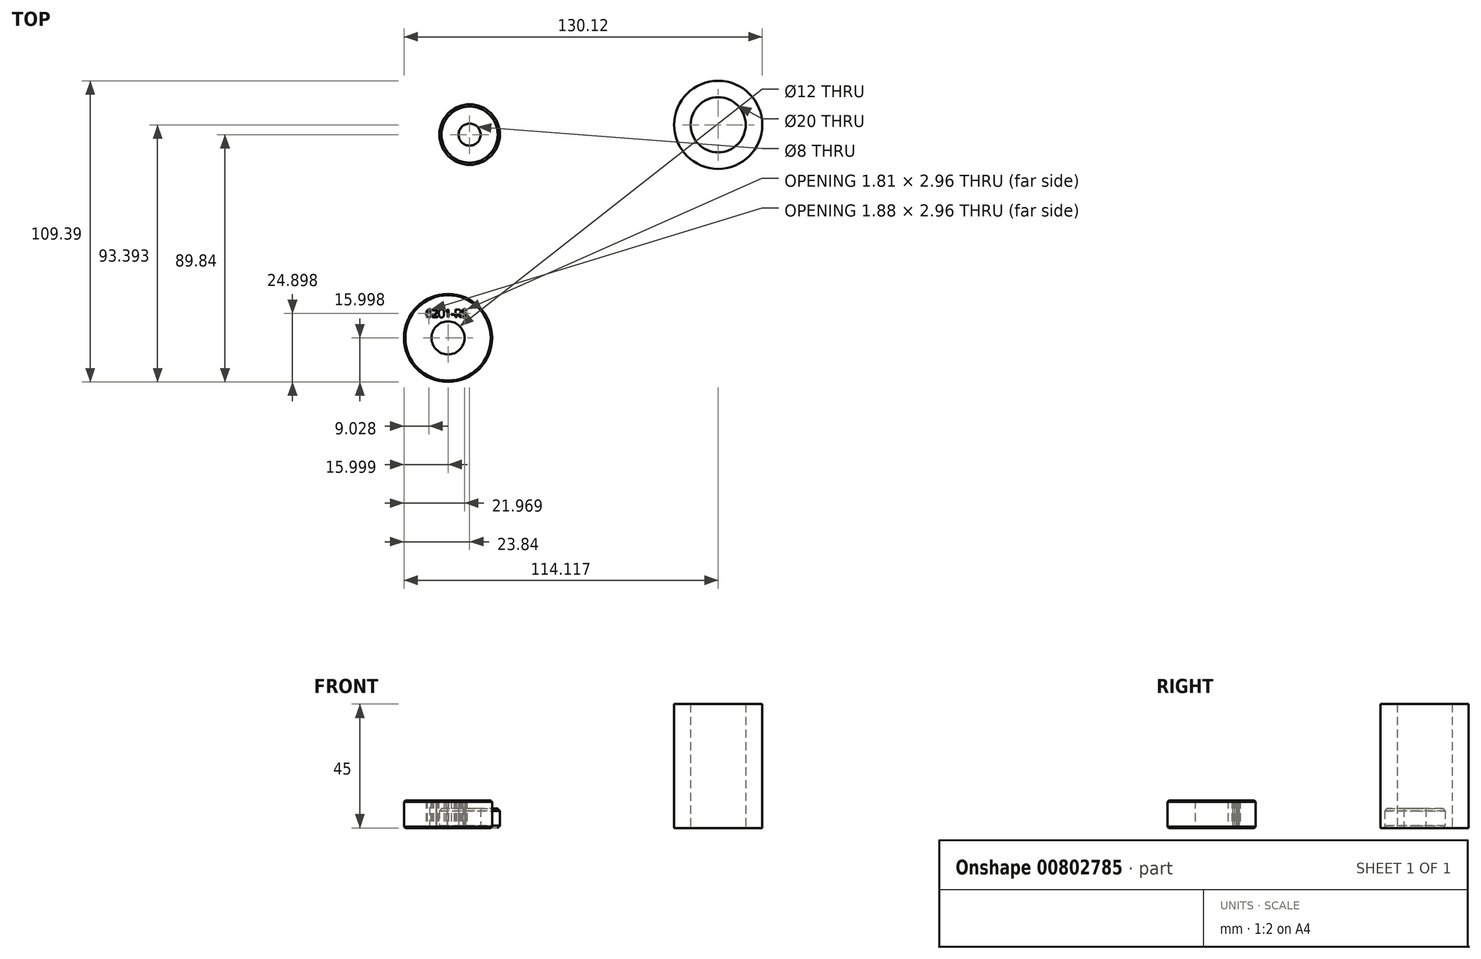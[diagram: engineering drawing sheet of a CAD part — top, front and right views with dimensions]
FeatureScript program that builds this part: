
annotation { "Feature Type Name" : "Feature", "Feature Type Description" : "" }
export const myFeature = defineFeature(function(context is Context, id is Id, definition is map)
    precondition{}
    {
        {
            var Q0;
            Q0=qCreatedBy(makeId("Top.planeOp"),FACE);
            var sketch = newSketch(context, id + "F0", { "sketchPlane" : qUnion([Q0])});
            skCircle(sketch, "E0", {"center": v(-54.52, 42.58) * mm, "radius": 4 * mm});
            skCircle(sketch, "E1", {"center": v(-54.52, 42.58) * mm, "radius": 11 * mm});
            skSolve(sketch);
        }
        {
            var Q0;
            Q0=makeQuery(id+"F0.imprint","IMPRINT",FACE,{"disambiguationData":[TD([[makeQuery(id+"F0.imprint","IMPRINT",EDGE,{"derivedFrom":sQuery(id+"F0.wireOp",EDGE,"E0")}),-1.0]])]});
            extrude(context, id + "F1", {"entities" : qUnion([Q0]), "depth" : 7 * mm});
        }
        {
            var Q0;
            Q0=makeQuery(id+"F1.opExtrude","CAP_EDGE",EDGE,{"disambiguationData":[OSD([sQuery(id+"F0.wireOp",EDGE,"E1")])],"isStart":false});
            var Q1;
            Q1=makeQuery(id+"F1.opExtrude","CAP_EDGE",EDGE,{"disambiguationData":[OSD([sQuery(id+"F0.wireOp",EDGE,"E1")])],"isStart":true});
            chamfer(context, id + "F2", {"entities" : qUnion([Q0, Q1]), "width" : .8 * mm, "tangentPropagation" : true});
        }
        {
            var Q0;
            Q0=qCreatedBy(makeId("Top.planeOp"),FACE);
            var sketch = newSketch(context, id + "F3", { "sketchPlane" : qUnion([Q0])});
            skCircle(sketch, "E2", {"center": v(35.76, 46.13) * mm, "radius": 10 * mm});
            skCircle(sketch, "E3", {"center": v(35.76, 46.13) * mm, "radius": 16 * mm});
            skSolve(sketch);
        }
        {
            var Q0;
            Q0=makeQuery(id+"F3.imprint","IMPRINT",FACE,{"disambiguationData":[TD([[makeQuery(id+"F3.imprint","IMPRINT",EDGE,{"derivedFrom":sQuery(id+"F3.wireOp",EDGE,"E2")}),-1.0]])]});
            extrude(context, id + "F4", {"entities" : qUnion([Q0]), "depth" : 45 * mm});
        }
        {
            var Q0;
            Q0=qCreatedBy(makeId("Top.planeOp"),FACE);
            var sketch = newSketch(context, id + "F5", { "sketchPlane" : qUnion([Q0])});
            skCircle(sketch, "E4", {"center": v(-62.36, -31.26) * mm, "radius": 6 * mm});
            skCircle(sketch, "E5", {"center": v(-62.36, -31.26) * mm, "radius": 16 * mm});
            skText(sketch, "E6", { "text": "6201-RS", "fontName": "OpenSans-Regular.ttf"});
            const initialGuessF5  = {"E6": [-0.0705, -0.0238, 1, 0, 0.0029]};
            skSetInitialGuess(sketch, initialGuessF5);
            skSolve(sketch);
        }
        {
            var Q0;
            Q0=qSketchRegion(id+"F5",true);
            extrude(context, id + "F6", {"entities" : qUnion([Q0]), "depth" : 10 * mm});
        }
        {
            var Q0;
            Q0=makeQuery(id+"F6.opExtrude","CAP_EDGE",EDGE,{"disambiguationData":[OSD([sQuery(id+"F5.wireOp",EDGE,"E5")])],"isStart":false});
            var Q1;
            Q1=makeQuery(id+"F6.opExtrude","CAP_EDGE",EDGE,{"disambiguationData":[OSD([sQuery(id+"F5.wireOp",EDGE,"E5")])],"isStart":true});
            chamfer(context, id + "F7", {"entities" : qUnion([Q0, Q1]), "width" : .5 * mm, "tangentPropagation" : true});
        }
    });
